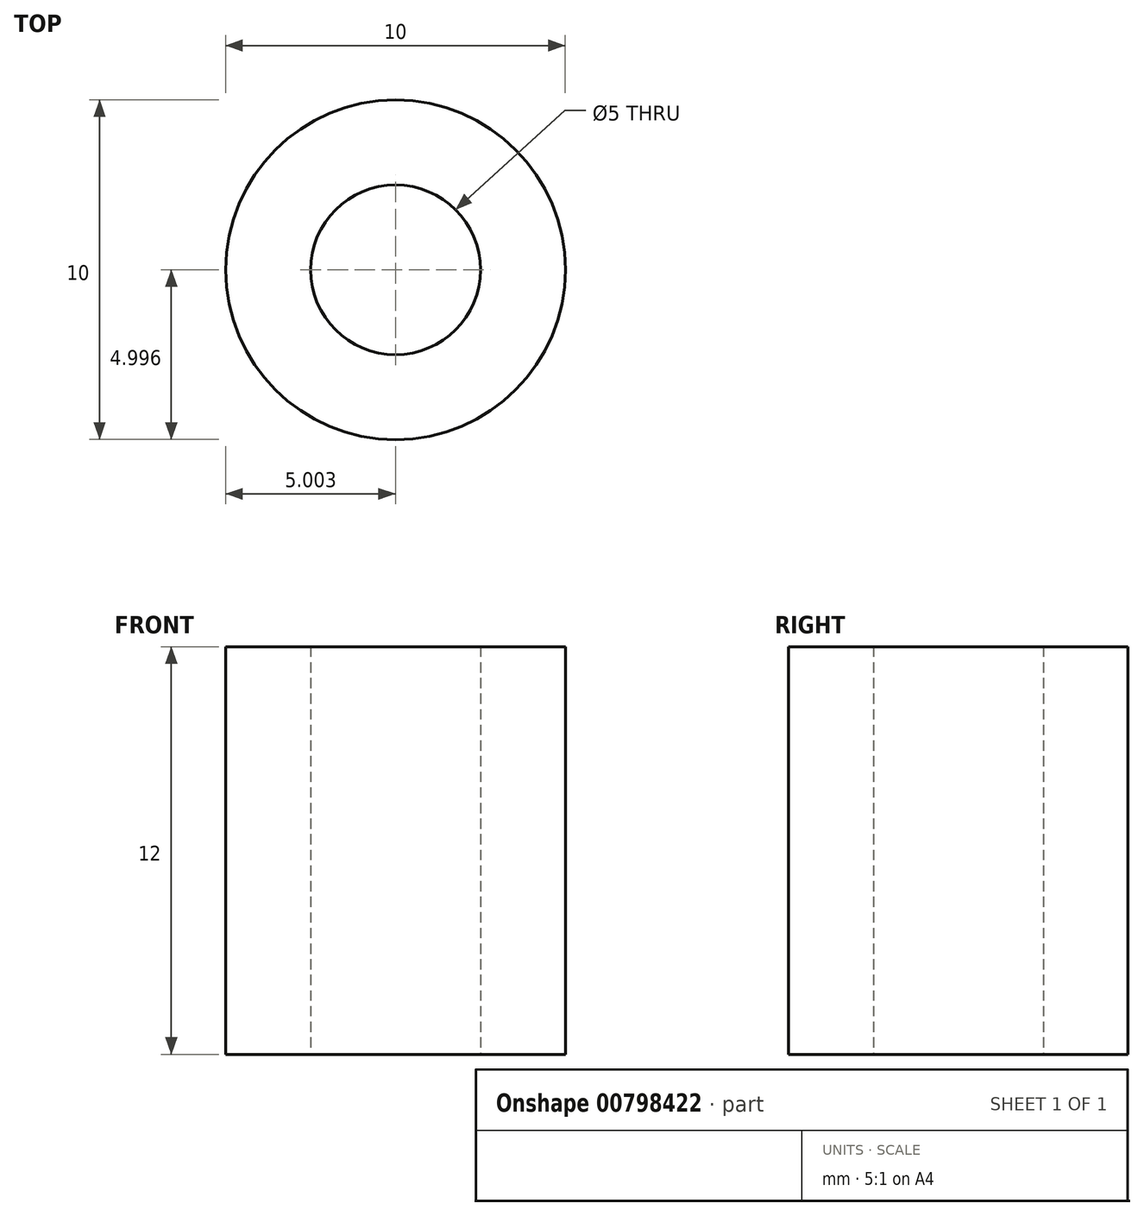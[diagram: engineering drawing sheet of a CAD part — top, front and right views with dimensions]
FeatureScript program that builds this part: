
annotation { "Feature Type Name" : "Feature", "Feature Type Description" : "" }
export const myFeature = defineFeature(function(context is Context, id is Id, definition is map)
    precondition{}
    {
        {
            var Q0;
            Q0=qCreatedBy(makeId("Top.planeOp"),FACE);
            var sketch = newSketch(context, id + "F0", { "sketchPlane" : qUnion([Q0])});
            skCircle(sketch, "E0", {"center": v(-20.25, 13.72) * mm, "radius": 5 * mm});
            skSolve(sketch);
        }
        {
            var Q0;
            Q0=makeQuery(id+"F0.imprint","IMPRINT",FACE,{"disambiguationData":[TD([[makeQuery(id+"F0.imprint","IMPRINT",EDGE,{"derivedFrom":sQuery(id+"F0.wireOp",EDGE,"E0")}),1.0]])]});
            extrude(context, id + "F1", {"entities" : qUnion([Q0]), "depth" : 12 * mm, "offsetDistance" : 25 * mm});
        }
        {
            var Q0;
            Q0=sQuery(id+"F0.wireOp",VERTEX,"E0.center");
            var Q1;
            Q1=makeQuery(id+"F1.opExtrude","SWEPT_BODY",BODY,{"disambiguationData":[OSD([sQuery(id+"F0.wireOp",EDGE,"E0")])]});
            hole(context, id + "F2", {"style" : HoleStyle.SIMPLE, "endStyle" : HoleEndStyle.THROUGH, "oppositeDirection" : true, "holeDiameter" : 5 * mm, "majorDiameter" : 5 * mm, "tappedDepth" : 12 * mm, "tapClearance" : 3, "locations" : qUnion([Q0]), "scope" : qUnion([Q1])});
        }
    });
